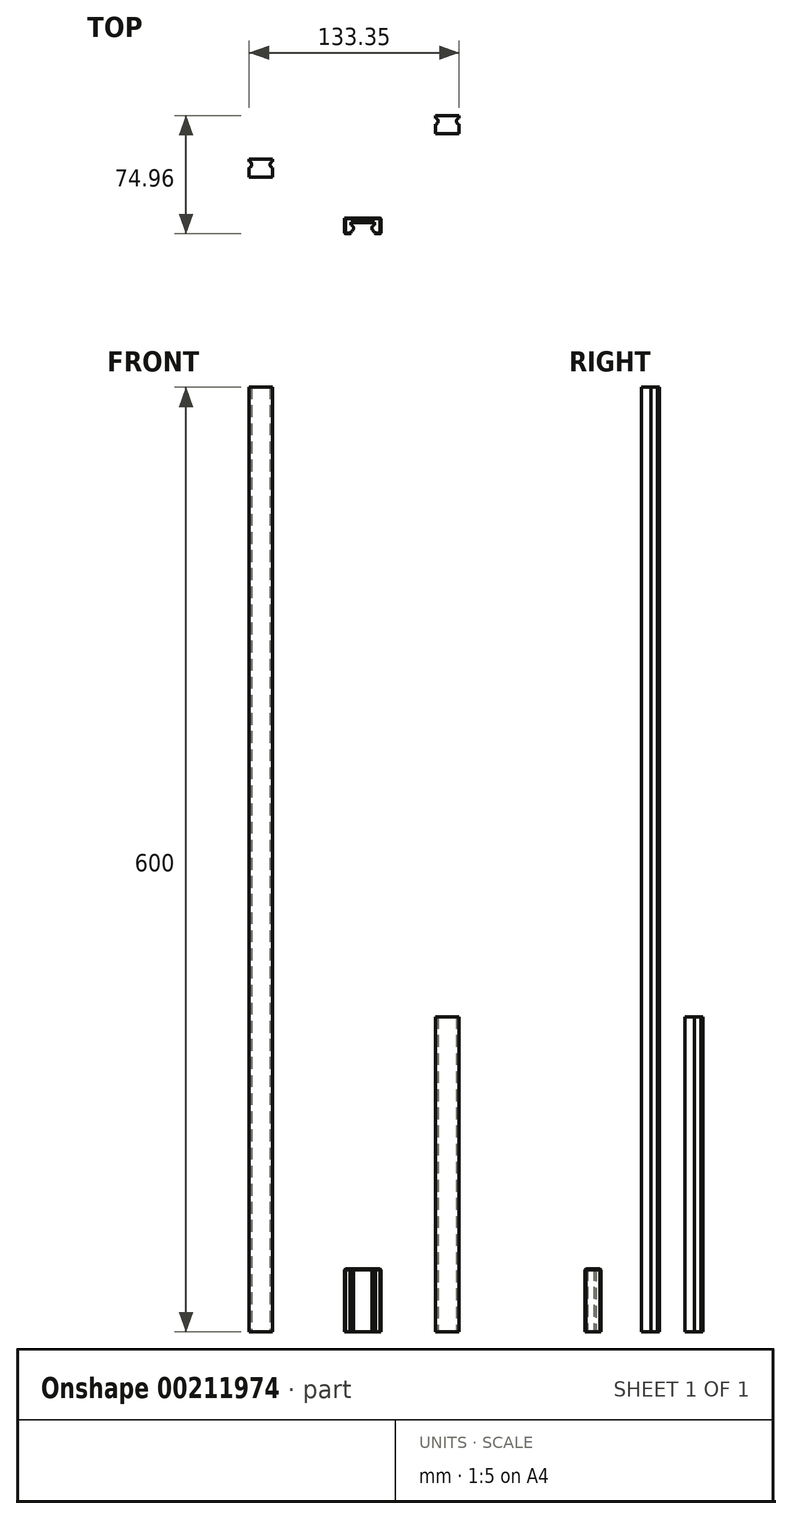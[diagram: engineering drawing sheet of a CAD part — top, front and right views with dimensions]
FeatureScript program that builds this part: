
annotation { "Feature Type Name" : "Feature", "Feature Type Description" : "" }
export const myFeature = defineFeature(function(context is Context, id is Id, definition is map)
    precondition{}
    {
        {
            var Q0;
            Q0=qCreatedBy(makeId("Top.planeOp"),FACE);
            var sketch = newSketch(context, id + "F0", { "sketchPlane" : qUnion([Q0])});
            skLineSegment(sketch, "E0", {"start": v(-54.8, 0) * mm, "end": v(-39.8, 0) * mm});
            skLineSegment(sketch, "E1", {"start": v(-39.8, 0) * mm, "end": v(-39.8, 6) * mm});
            skLineSegment(sketch, "E2", {"start": v(-54.8, 0) * mm, "end": v(-54.8, 6) * mm});
            skArc(sketch, "E3", {"start": v(-54.8, 6) * mm, "mid": v(-53.13, 8) * mm, "end": v(-54.8, 10) * mm});
            skArc(sketch, "E4", {"start": v(-39.8, 10) * mm, "mid": v(-41.48, 8) * mm, "end": v(-39.8, 6) * mm});
            skLineSegment(sketch, "E5", {"start": v(-54.8, 10) * mm, "end": v(-54.8, 11.5) * mm});
            skLineSegment(sketch, "E6", {"start": v(-54.8, 11.5) * mm, "end": v(-39.8, 11.5) * mm});
            skLineSegment(sketch, "E7", {"start": v(-39.8, 11.5) * mm, "end": v(-39.8, 10) * mm});
            skLineSegment(sketch, "E8", {"start": v(63.54, 27.57) * mm, "end": v(78.54, 27.57) * mm});
            skLineSegment(sketch, "E9", {"start": v(78.54, 27.57) * mm, "end": v(78.54, 33.57) * mm});
            skLineSegment(sketch, "E10", {"start": v(63.54, 27.57) * mm, "end": v(63.54, 33.57) * mm});
            skArc(sketch, "E11", {"start": v(63.54, 33.57) * mm, "mid": v(65.21, 35.57) * mm, "end": v(63.54, 37.57) * mm});
            skArc(sketch, "E12", {"start": v(78.54, 37.57) * mm, "mid": v(76.87, 35.57) * mm, "end": v(78.54, 33.57) * mm});
            skLineSegment(sketch, "E13", {"start": v(63.54, 37.57) * mm, "end": v(63.54, 39.07) * mm});
            skLineSegment(sketch, "E14", {"start": v(63.54, 39.07) * mm, "end": v(78.54, 39.07) * mm});
            skLineSegment(sketch, "E15", {"start": v(78.54, 39.07) * mm, "end": v(78.54, 37.57) * mm});
            skLineSegment(sketch, "E16", {"start": v(9.83, -40.4) * mm, "end": v(24.83, -40.4) * mm});
            skLineSegment(sketch, "E17", {"start": v(24.83, -40.4) * mm, "end": v(24.83, -34.4) * mm});
            skLineSegment(sketch, "E18", {"start": v(9.83, -40.4) * mm, "end": v(9.83, -34.4) * mm});
            skArc(sketch, "E19", {"start": v(9.83, -34.4) * mm, "mid": v(11.5, -32.4) * mm, "end": v(9.83, -30.4) * mm});
            skArc(sketch, "E20", {"start": v(24.83, -30.4) * mm, "mid": v(23.16, -32.4) * mm, "end": v(24.83, -34.4) * mm});
            skLineSegment(sketch, "E21", {"start": v(9.83, -30.4) * mm, "end": v(9.83, -28.9) * mm});
            skLineSegment(sketch, "E22", {"start": v(9.83, -28.9) * mm, "end": v(24.83, -28.9) * mm});
            skLineSegment(sketch, "E23", {"start": v(24.83, -28.9) * mm, "end": v(24.83, -30.4) * mm});
            skLineSegment(sketch, "E24", {"start": v(9.83, -35.9) * mm, "end": v(5.83, -35.9) * mm});
            skLineSegment(sketch, "E25", {"start": v(5.83, -35.9) * mm, "end": v(5.83, -25.9) * mm});
            skLineSegment(sketch, "E26", {"start": v(5.83, -25.9) * mm, "end": v(28.83, -25.9) * mm});
            skLineSegment(sketch, "E27", {"start": v(28.83, -25.9) * mm, "end": v(28.83, -35.9) * mm});
            skLineSegment(sketch, "E28", {"start": v(28.83, -35.9) * mm, "end": v(24.83, -35.9) * mm});
            skSolve(sketch);
        }
        {
            var Q0;
            Q0=makeQuery(id+"F0.imprint","IMPRINT",FACE,{"disambiguationData":[TD([[makeQuery(id+"F0.imprint","IMPRINT",EDGE,{"derivedFrom":sQuery(id+"F0.wireOp",EDGE,"E0")}),1.0]])]});
            extrude(context, id + "F1", {"entities" : qUnion([Q0]), "depth" : 600 * mm});
        }
        {
            var Q0;
            Q0=makeQuery(id+"F0.imprint","IMPRINT",FACE,{"disambiguationData":[TD([[makeQuery(id+"F0.imprint","IMPRINT",EDGE,{"derivedFrom":sQuery(id+"F0.wireOp",EDGE,"E8")}),1.0]])]});
            var Q1;
            Q1=sQuery(id+"F0.wireOp",EDGE,"E8");
            var Q2;
            Q2=sQuery(id+"F0.wireOp",EDGE,"E9");
            var Q3;
            Q3=sQuery(id+"F0.wireOp",EDGE,"E10");
            var Q4;
            Q4=sQuery(id+"F0.wireOp",EDGE,"E11");
            var Q5;
            Q5=sQuery(id+"F0.wireOp",EDGE,"E12");
            var Q6;
            Q6=sQuery(id+"F0.wireOp",EDGE,"E13");
            var Q7;
            Q7=sQuery(id+"F0.wireOp",EDGE,"E14");
            var Q8;
            Q8=sQuery(id+"F0.wireOp",EDGE,"E15");
            extrude(context, id + "F2", {"entities" : qUnion([Q0]), "surfaceEntities" : qUnion([Q1, Q2, Q3, Q4, Q5, Q6, Q7, Q8]), "depth" : 200 * mm});
        }
        {
            var Q0;
            {var subQ4=sQuery(id+"F0.wireOp",EDGE,"E19");Q0=makeQuery(id+"F0.imprint","IMPRINT",FACE,{"disambiguationData":[TD([[makeQuery(id+"F0.imprint","IMPRINT",EDGE,{"derivedFrom":subQ4}),1.0]])]});}
            extrude(context, id + "F3", {"entities" : qUnion([Q0]), "depth" : 40 * mm});
        }
        {
            var Q0;
            Q0=makeQuery(id+"F3.opExtrude","CAP_EDGE",EDGE,{"disambiguationData":[OSD([sQuery(id+"F0.wireOp",EDGE,"E26")])],"isStart":false});
            var Q1;
            Q1=makeQuery(id+"F3.opExtrude","CAP_EDGE",EDGE,{"disambiguationData":[OSD([sQuery(id+"F0.wireOp",EDGE,"E25")])],"isStart":false});
            var Q2;
            Q2=makeQuery(id+"F3.opExtrude","CAP_EDGE",EDGE,{"disambiguationData":[OSD([sQuery(id+"F0.wireOp",EDGE,"E27")])],"isStart":false});
            var Q3;
            Q3=makeQuery(id+"F3.opExtrude","CAP_EDGE",EDGE,{"disambiguationData":[OSD([sQuery(id+"F0.wireOp",EDGE,"E24")])],"isStart":false});
            var Q4;
            Q4=makeQuery(id+"F3.opExtrude","CAP_EDGE",EDGE,{"disambiguationData":[OSD([sQuery(id+"F0.wireOp",EDGE,"E28")])],"isStart":false});
            var Q5;
            Q5=makeQuery(id+"F3.opExtrude","SWEPT_EDGE",EDGE,{"disambiguationData":[OSD([sQuery(id+"F0.wireOp",EDGE,"E24"),sQuery(id+"F0.wireOp",EDGE,"E25")])]});
            var Q6;
            Q6=makeQuery(id+"F3.opExtrude","SWEPT_EDGE",EDGE,{"disambiguationData":[OSD([sQuery(id+"F0.wireOp",EDGE,"E27"),sQuery(id+"F0.wireOp",EDGE,"E28")])]});
            var Q7;
            Q7=makeQuery(id+"F3.opExtrude","SWEPT_EDGE",EDGE,{"disambiguationData":[OSD([sQuery(id+"F0.wireOp",EDGE,"E26"),sQuery(id+"F0.wireOp",EDGE,"E27")])]});
            var Q8;
            Q8=makeQuery(id+"F3.opExtrude","CAP_EDGE",EDGE,{"disambiguationData":[OSD([sQuery(id+"F0.wireOp",EDGE,"E22")])],"isStart":false});
            var Q9;
            Q9=makeQuery(id+"F3.opExtrude","SWEPT_EDGE",EDGE,{"disambiguationData":[OSD([sQuery(id+"F0.wireOp",EDGE,"E18"),sQuery(id+"F0.wireOp",EDGE,"E24")])]});
            var Q10;
            Q10=makeQuery(id+"F3.opExtrude","SWEPT_EDGE",EDGE,{"disambiguationData":[OSD([sQuery(id+"F0.wireOp",EDGE,"E17"),sQuery(id+"F0.wireOp",EDGE,"E28")])]});
            chamfer(context, id + "F4", {"entities" : qUnion([Q0, Q1, Q2, Q3, Q4, Q5, Q6, Q7, Q8, Q9, Q10]), "width" : 0.5 * mm, "tangentPropagation" : true});
        }
    });
